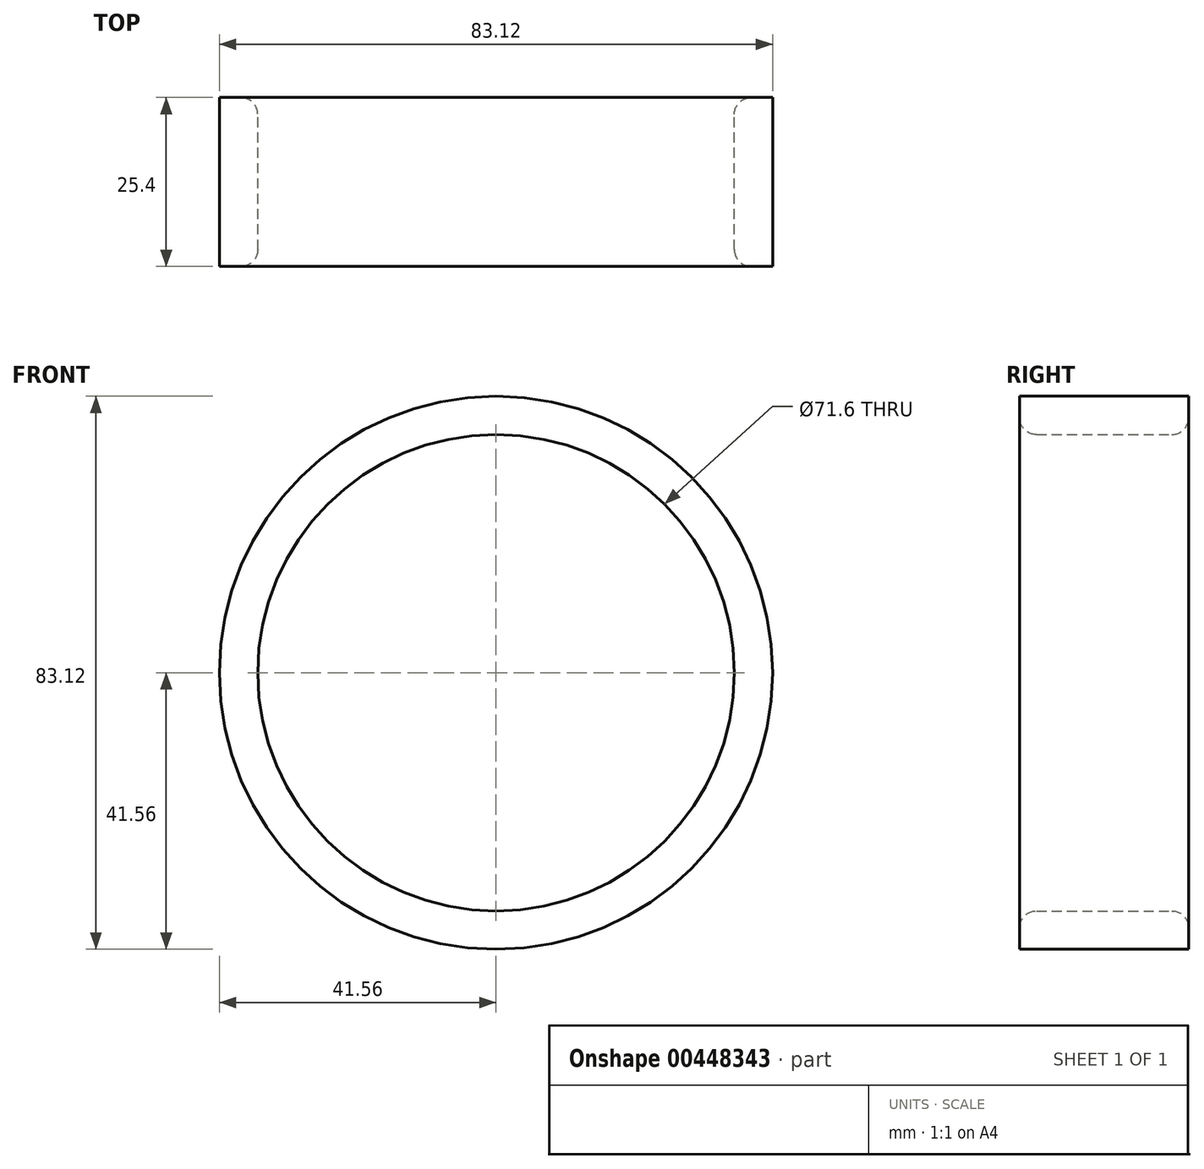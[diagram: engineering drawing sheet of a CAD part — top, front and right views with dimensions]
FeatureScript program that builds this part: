
annotation { "Feature Type Name" : "Feature", "Feature Type Description" : "" }
export const myFeature = defineFeature(function(context is Context, id is Id, definition is map)
    precondition{}
    {
        {
            var Q0;
            Q0=qCreatedBy(makeId("Front.planeOp"),FACE);
            var sketch = newSketch(context, id + "F0", { "sketchPlane" : qUnion([Q0])});
            skCircle(sketch, "E0", {"center": v(0, 0) * mm, "radius": 41.56 * mm});
            skCircle(sketch, "E1", {"center": v(0, 0) * mm, "radius": 35.8 * mm});
            skSolve(sketch);
        }
        {
            var Q0;
            Q0 = qBodyType(qCreatedBy(id + "F0" ,EDGE), BodyType.WIRE);
            var sketch = newSketch(context, id + "F1", { "sketchPlane" : qUnion([Q0])});
            skSolve(sketch);
        }
        {
            var Q0;
            Q0 = qSketchRegion(id + "F1", true);
            var Q1;
            Q1=makeQuery(id+"F0.imprint","IMPRINT",FACE,{"disambiguationData":[TD([[makeQuery(id+"F0.imprint","IMPRINT",EDGE,{"derivedFrom":sQuery(id+"F0.wireOp",EDGE,"E0")}),1.0]])]});
            extrude(context, id + "F2", {"entities" : qUnion([Q0, Q1]), "depth" : 25.4 * mm});
        }
        {
            var Q0;
            Q0=makeQuery(id+"F2.opExtrude","CAP_EDGE",EDGE,{"disambiguationData":[OSD([sQuery(id+"F0.wireOp",EDGE,"E1")])],"isStart":false});
            fillet(context, id + "F3", {"entities" : qUnion([Q0]), "radius" : 2.54 * mm, "tangentPropagation" : true, "allowEdgeOverflow" : false});
        }
        {
            var Q0;
            Q0=makeQuery(id+"F2.opExtrude","CAP_EDGE",EDGE,{"disambiguationData":[OSD([sQuery(id+"F0.wireOp",EDGE,"E1")])],"isStart":true});
            fillet(context, id + "F4", {"entities" : qUnion([Q0]), "radius" : 2.54 * mm, "tangentPropagation" : true, "allowEdgeOverflow" : false});
        }
    });
